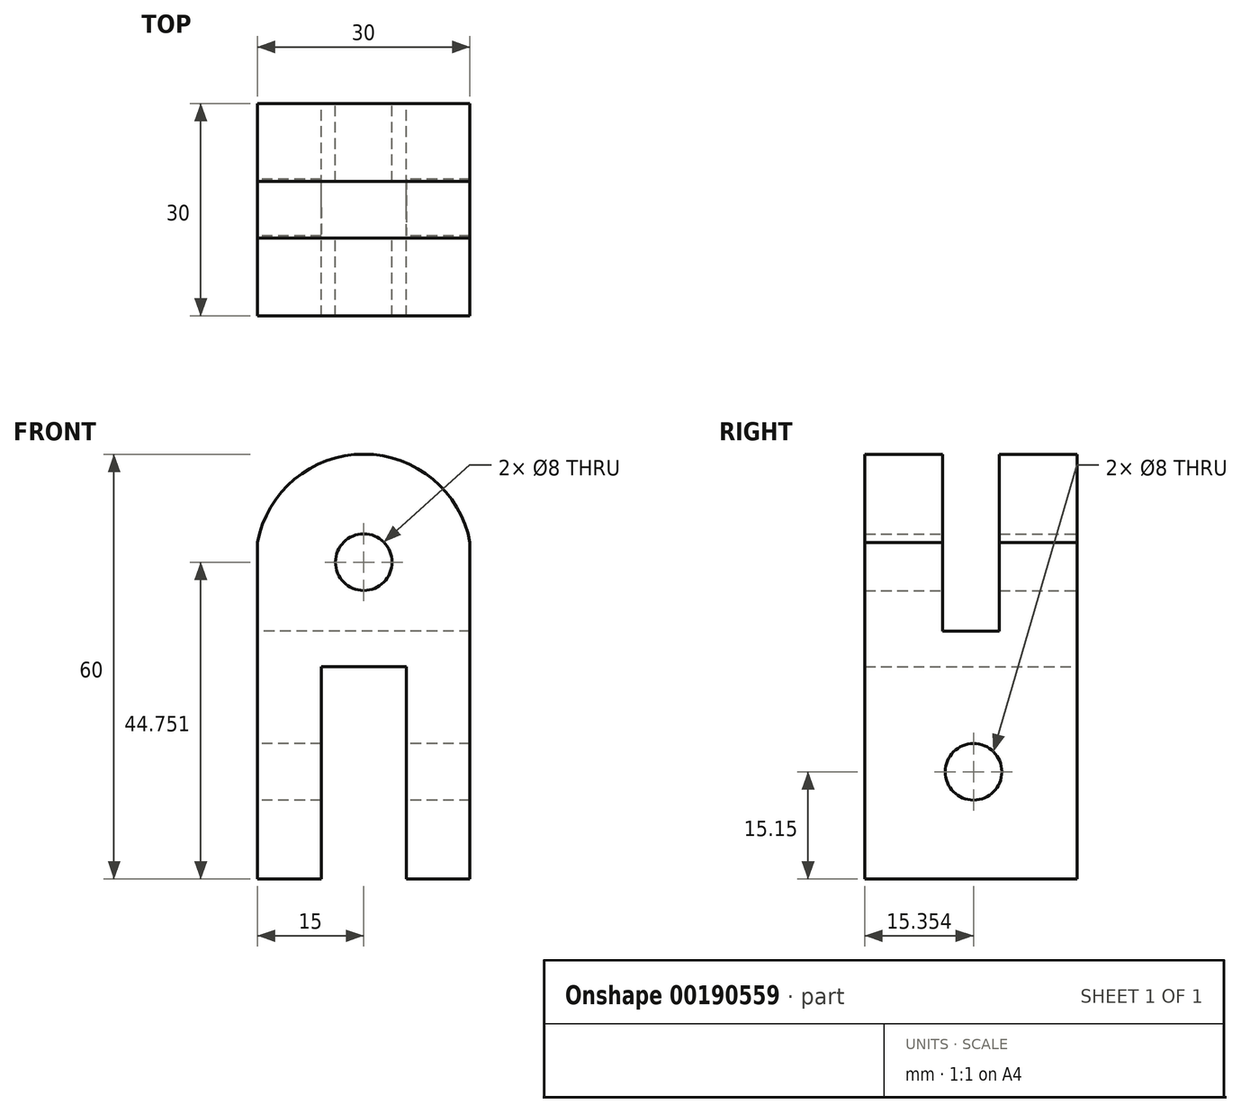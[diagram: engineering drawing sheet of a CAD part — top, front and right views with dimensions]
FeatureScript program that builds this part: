
annotation { "Feature Type Name" : "Feature", "Feature Type Description" : "" }
export const myFeature = defineFeature(function(context is Context, id is Id, definition is map)
    precondition{}
    {
        {
            var Q0;
            Q0=qCreatedBy(makeId("Front.planeOp"),FACE);
            var sketch = newSketch(context, id + "F0", { "sketchPlane" : qUnion([Q0])});
            skLineSegment(sketch, "E0.bottom", {"start": v(-15, 30) * mm, "end": v(15, 30) * mm});
            skLineSegment(sketch, "E0.top", {"start": v(-15, -30) * mm, "end": v(-6, -30) * mm});
            skLineSegment(sketch, "E0.left", {"start": v(-15, 30) * mm, "end": v(-15, -30) * mm});
            skLineSegment(sketch, "E0.right", {"start": v(15, 30) * mm, "end": v(15, -30) * mm});
            skPoint(sketch, "E0.middle", {"position": v(0, 0) * mm});
            skLineSegment(sketch, "E1.bottom", {"start": v(-6, 0) * mm, "end": v(6, 0) * mm});
            skLineSegment(sketch, "E1.left", {"start": v(-6, 0) * mm, "end": v(-6, -30) * mm});
            skLineSegment(sketch, "E1.right", {"start": v(6, 0) * mm, "end": v(6, -30) * mm});
            skLineSegment(sketch, "E2", {"start": v(6, -30) * mm, "end": v(15, -30) * mm});
            skSolve(sketch);
        }
        {
            var Q0;
            Q0 = qSketchRegion(id + "F0", true);
            extrude(context, id + "F1", {"entities" : qUnion([Q0]), "depth" : 30 * mm});
        }
        {
            var Q0;
            Q0=makeQuery(id+"F1.opExtrude","SWEPT_FACE",FACE,{"disambiguationData":[OSD([sQuery(id+"F0.wireOp",EDGE,"E0.left")])]});
            var sketch = newSketch(context, id + "F2", { "sketchPlane" : qUnion([Q0])});
            skCircle(sketch, "E3", {"center": v(14.65, -14.85) * mm, "radius": 4 * mm});
            skLineSegment(sketch, "E4.bottom", {"start": v(19, 5) * mm, "end": v(11, 5) * mm});
            skLineSegment(sketch, "E4.top", {"start": v(19, 55) * mm, "end": v(11, 55) * mm});
            skLineSegment(sketch, "E4.left", {"start": v(19, 5) * mm, "end": v(19, 55) * mm});
            skLineSegment(sketch, "E4.right", {"start": v(11, 5) * mm, "end": v(11, 55) * mm});
            skPoint(sketch, "E4.middle", {"position": v(15, 30) * mm});
            skSolve(sketch);
        }
        {
            var Q0;
            Q0 = qSketchRegion(id + "F2", true);
            extrude(context, id + "F3", {"entities" : qUnion([Q0]), "operationType" : NewBodyOperationType.REMOVE, "endBound" : BoundingType.THROUGH_ALL, "oppositeDirection" : true, "depth" : 25.4 * mm});
        }
        {
            var Q0;
            Q0=makeQuery(id+"F1.opExtrude","CAP_FACE",FACE,{"disambiguationData":[OSD([sQuery(id+"F0.wireOp",EDGE,"E0.bottom"),sQuery(id+"F0.wireOp",EDGE,"E0.top"),sQuery(id+"F0.wireOp",EDGE,"E0.left"),sQuery(id+"F0.wireOp",EDGE,"E0.right"),sQuery(id+"F0.wireOp",EDGE,"E1.bottom"),sQuery(id+"F0.wireOp",EDGE,"E1.left"),sQuery(id+"F0.wireOp",EDGE,"E1.right"),sQuery(id+"F0.wireOp",EDGE,"E2")])],"isStart":true});
            var sketch = newSketch(context, id + "F4", { "sketchPlane" : qUnion([Q0])});
            skCircle(sketch, "E5", {"center": v(0, 14.75) * mm, "radius": 4 * mm});
            skSolve(sketch);
        }
        {
            var Q0;
            Q0 = qSketchRegion(id + "F4", true);
            extrude(context, id + "F5", {"entities" : qUnion([Q0]), "operationType" : NewBodyOperationType.REMOVE, "endBound" : BoundingType.THROUGH_ALL, "oppositeDirection" : true, "depth" : 25.4 * mm});
        }
        {
            var Q0;
            Q0=makeQuery(id+"F1.opExtrude","CAP_FACE",FACE,{"disambiguationData":[OSD([sQuery(id+"F0.wireOp",EDGE,"E0.bottom"),sQuery(id+"F0.wireOp",EDGE,"E0.top"),sQuery(id+"F0.wireOp",EDGE,"E0.left"),sQuery(id+"F0.wireOp",EDGE,"E0.right"),sQuery(id+"F0.wireOp",EDGE,"E1.bottom"),sQuery(id+"F0.wireOp",EDGE,"E1.left"),sQuery(id+"F0.wireOp",EDGE,"E1.right"),sQuery(id+"F0.wireOp",EDGE,"E2")])],"isStart":true});
            var sketch = newSketch(context, id + "F6", { "sketchPlane" : qUnion([Q0])});
            skCircle(sketch, "E6", {"center": v(0, 14.75) * mm, "radius": 15.25 * mm});
            skSolve(sketch);
        }
        {
            var Q0;
            {var subQ0=sQuery(id+"F6.wireOp",EDGE,"E6");var subQ1=makeQuery(id+"F1.opExtrude","CAP_EDGE",EDGE,{"disambiguationData":[OSD([sQuery(id+"F0.wireOp",EDGE,"E0.bottom")])],"isStart":true});var subQ2=makeQuery(id+"F6.imprint","INTERSECT",VERTEX,{"derivedFrom":[subQ1,subQ0]});Q0=makeQuery(id+"F6.imprint","IMPRINT",FACE,{"disambiguationData":[TD([[makeQuery(id+"F6.imprint","IMPRINT",EDGE,{"disambiguationData":[TD([[subQ2,-1.0]])],"derivedFrom":subQ0}),-1.0]])]});}
            var Q1;
            {var subQ0=sQuery(id+"F6.wireOp",EDGE,"E6");var subQ1=makeQuery(id+"F1.opExtrude","CAP_EDGE",EDGE,{"disambiguationData":[OSD([sQuery(id+"F0.wireOp",EDGE,"E0.bottom")])],"isStart":true});var subQ2=makeQuery(id+"F6.imprint","INTERSECT",VERTEX,{"derivedFrom":[subQ1,subQ0]});Q1=makeQuery(id+"F6.imprint","IMPRINT",FACE,{"disambiguationData":[TD([[makeQuery(id+"F6.imprint","IMPRINT",EDGE,{"disambiguationData":[TD([[subQ2,1.0]])],"derivedFrom":subQ0}),-1.0]])]});}
            extrude(context, id + "F7", {"entities" : qUnion([Q0, Q1]), "operationType" : NewBodyOperationType.REMOVE, "endBound" : BoundingType.THROUGH_ALL, "oppositeDirection" : true, "depth" : 25.4 * mm});
        }
    });
